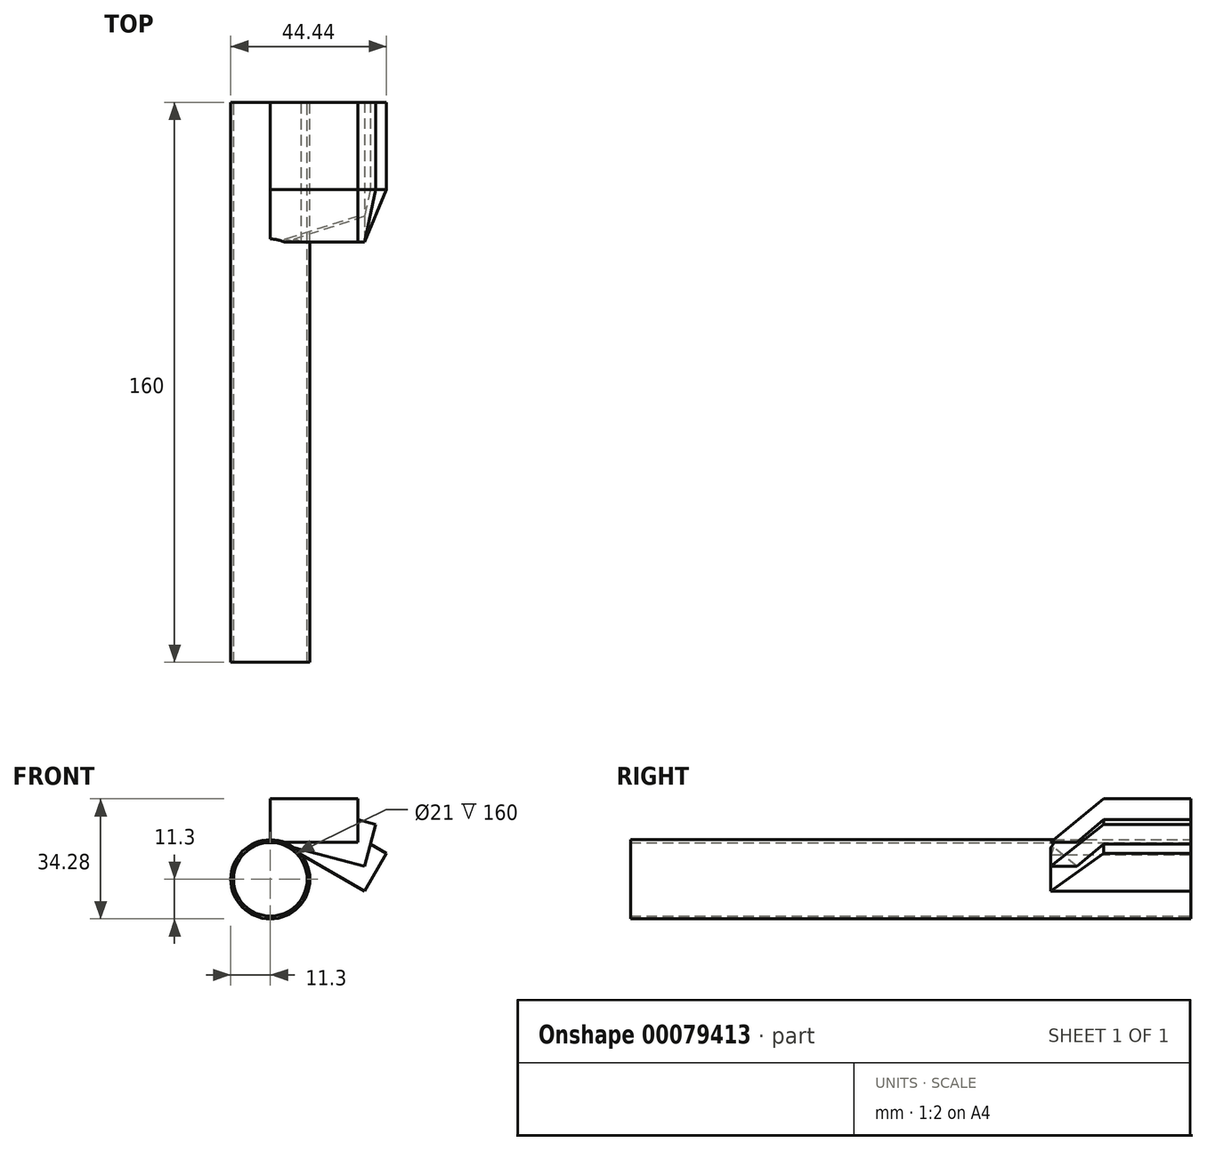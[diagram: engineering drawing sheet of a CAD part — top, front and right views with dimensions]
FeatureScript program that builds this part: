
annotation { "Feature Type Name" : "Feature", "Feature Type Description" : "" }
export const myFeature = defineFeature(function(context is Context, id is Id, definition is map)
    precondition{}
    {
        {
            var Q0;
            Q0=qCreatedBy(makeId("Front.planeOp"),FACE);
            var sketch = newSketch(context, id + "F0", { "sketchPlane" : qUnion([Q0])});
            skCircle(sketch, "E0", {"center": v(0, 0) * mm, "radius": 10.5 * mm});
            skCircle(sketch, "E1", {"center": v(0, 0) * mm, "radius": 11.3 * mm});
            skSolve(sketch);
        }
        {
            var Q0;
            Q0=makeQuery(id+"F0.imprint","IMPRINT",FACE,{"disambiguationData":[TD([[makeQuery(id+"F0.imprint","IMPRINT",EDGE,{"derivedFrom":sQuery(id+"F0.wireOp",EDGE,"E0")}),-1.0]])]});
            extrude(context, id + "F1", {"entities" : qUnion([Q0]), "depth" : 160 * mm});
        }
        {
            var Q0;
            Q0=qCreatedBy(makeId("Right.planeOp"),FACE);
            var sketch = newSketch(context, id + "F2", { "sketchPlane" : qUnion([Q0])});
            skLineSegment(sketch, "E2", {"start": v(0, 10.54) * mm, "end": v(-40, 10.54) * mm});
            skLineSegment(sketch, "E3", {"start": v(-40, 10.54) * mm, "end": v(-24.98, 22.98) * mm});
            skLineSegment(sketch, "E4", {"start": v(-24.98, 22.98) * mm, "end": v(0, 22.98) * mm});
            skLineSegment(sketch, "E5", {"start": v(0, 22.98) * mm, "end": v(0, 10.54) * mm});
            skSolve(sketch);
        }
        {
            var Q0;
            Q0=makeQuery(id+"F2.imprint","IMPRINT",FACE,{"disambiguationData":[TD([[makeQuery(id+"F2.imprint","IMPRINT",EDGE,{"derivedFrom":sQuery(id+"F2.wireOp",EDGE,"E2")}),-1.0]])]});
            extrude(context, id + "F3", {"entities" : qUnion([Q0]), "operationType" : NewBodyOperationType.ADD, "depth" : 25 * mm});
        }
        {
            var Q0;
            Q0=makeQuery(id+"F1.opExtrude","SWEPT_BODY",BODY,{"disambiguationData":[OSD([sQuery(id+"F0.wireOp",EDGE,"E0"),sQuery(id+"F0.wireOp",EDGE,"E1")])]});
            var Q1;
            Q1=makeQuery(id+"F1.opExtrude","SWEPT_FACE",FACE,{"disambiguationData":[OSD([sQuery(id+"F0.wireOp",EDGE,"E1")])]});
            circularPattern(context, id + "F4", {"operationType" : NewBodyOperationType.ADD, "entities" : qUnion([Q0]), "axis" : qUnion([Q1]), "angle" : 30 * degree, "instanceCount" : 3, "equalSpace" : true});
        }
    });
